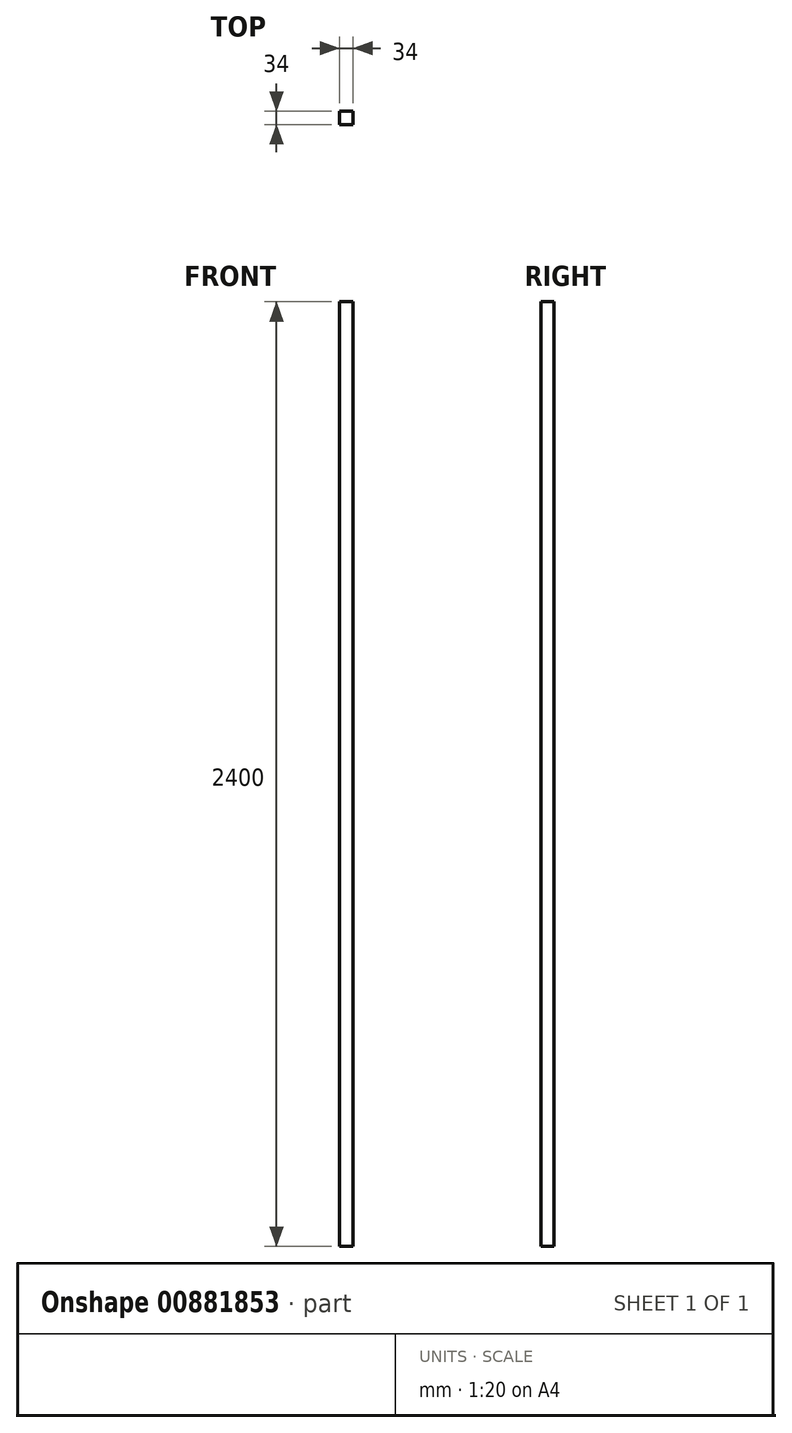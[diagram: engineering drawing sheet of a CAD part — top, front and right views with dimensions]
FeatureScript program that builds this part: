
annotation { "Feature Type Name" : "Feature", "Feature Type Description" : "" }
export const myFeature = defineFeature(function(context is Context, id is Id, definition is map)
    precondition{}
    {
        {
            var Q0;
            Q0=qCreatedBy(makeId("Top.planeOp"),FACE);
            var sketch = newSketch(context, id + "F0", { "sketchPlane" : qUnion([Q0])});
            skLineSegment(sketch, "E0.bottom", {"start": v(17, -17) * mm, "end": v(-17, -17) * mm});
            skLineSegment(sketch, "E0.top", {"start": v(17, 17) * mm, "end": v(-17, 17) * mm});
            skLineSegment(sketch, "E0.left", {"start": v(17, -17) * mm, "end": v(17, 17) * mm});
            skLineSegment(sketch, "E0.right", {"start": v(-17, -17) * mm, "end": v(-17, 17) * mm});
            skPoint(sketch, "E0.middle", {"position": v(0, 0) * mm});
            skSolve(sketch);
        }
        {
            var Q0;
            Q0=qSketchRegion(id+"F0",true);
            extrude(context, id + "F1", {"entities" : qUnion([Q0]), "depth" : 2400 * mm, "offsetDistance" : 25 * mm});
        }
    });
